# Revit family: EKF_EE_РейкаМонтажнаяПерфорированнаяUNIT_PROxima
name_source: partatom
category: Электрооборудование
units: mm (PartAtom-declared; Revit-internal decimal feet)

## family parameters
Всегда вертикально = Нет
На основе рабочей плоскости = Да
Общий = Да
При загрузке вырезать с полостями = Нет
Размер круглого соединителя = Использовать диаметр
Тип детали = Силовой щит
Точка расчета площади = Нет

## types (4) — shared parameters
ADSK_Единица измерения = шт.
ADSK_Завод-изготовитель = EKF
ADSK_Количество = 1
ADSK_Марка = Рейка монтажная
ADSK_Материал = Сталь_Оцинкованная
ADSK_Обозначение = Рейка монтажная
ADSK_Размер_Высота = 50 мм
ADSK_Размер_Глубина = 10 мм
t = 1 мм
Изготовитель = EKF
Серия номенклатуры = Unit PROxima
Степень защиты IP = -
ТВ = EKF_2
Тип установки = -
zero-valued in all types: ADSK_Масса, Отметка по умолчанию

## per-type parameters (varying)
| type | ADSK_Код изделия | ADSK_Размер_Ширина | Отступ | Тип | Шаг |
| Рейка монтажная (50x360) перфорированная к ВРУ Unit (Вх450хГ) EKF PROxima | mb15-04-02 | 360 мм | 27 мм | 68 мм | 34 мм |
| Рейка монтажная (50x510) перфорированная к ВРУ Unit и ЩО-70  (Вх600хГ) EKF PROxima | mb15-05-02 | 510 мм | 27.5 мм | 69 мм | 35 мм |
| Рейка монтажная (50x710) перфорированная к ВРУ Unit и ЩО-70 (Вх800хГ) EKF PROxima | mb15-06-02 | 710 мм | 22.5 мм | 70 мм | 35 мм |
| Рейка монтажная (50x910) перфорированная к ВРУ Unit и ЩО-70 (Вх1000хГ) EKF PROxima | mb15-10-02 | 910 мм | 30 мм | 71 мм | 34 мм |

note: column(s) folded — value = type name in every type: ADSK_Наименование
